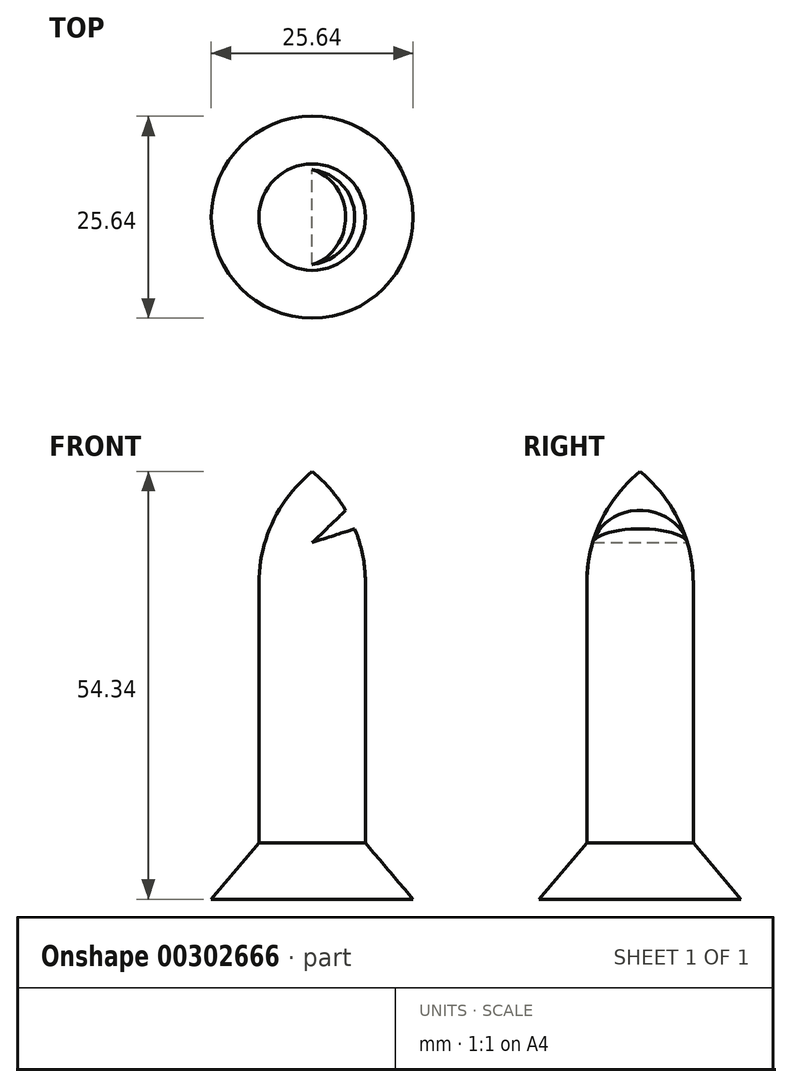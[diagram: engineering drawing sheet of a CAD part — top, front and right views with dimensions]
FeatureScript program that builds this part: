
annotation { "Feature Type Name" : "Feature", "Feature Type Description" : "" }
export const myFeature = defineFeature(function(context is Context, id is Id, definition is map)
    precondition{}
    {
        {
            var Q0;
            Q0=qCreatedBy(makeId("Front.planeOp"),FACE);
            var sketch = newSketch(context, id + "F0", { "sketchPlane" : qUnion([Q0])});
            skLineSegment(sketch, "E0", {"start": v(0, 0) * mm, "end": v(0, 0) * mm});
            skLineSegment(sketch, "E1", {"start": v(0, 54.34) * mm, "end": v(0, 0) * mm});
            skLineSegment(sketch, "E2", {"start": v(0, 40.14) * mm, "end": v(6.76, 40.14) * mm});
            skLineSegment(sketch, "E3", {"start": v(6.76, 40.14) * mm, "end": v(6.76, 7.16) * mm});
            skLineSegment(sketch, "E4", {"start": v(6.76, 7.16) * mm, "end": v(12.82, 0) * mm});
            skLineSegment(sketch, "E5", {"start": v(12.82, 0) * mm, "end": v(0, 0) * mm});
            skArc(sketch, "E6", {"start": v(6.76, 40.14) * mm, "mid": v(4.98, 48) * mm, "end": v(0, 54.34) * mm});
            skSolve(sketch);
        }
        {
            var Q0;
            Q0 = qSketchRegion(id + "F0", true);
            var Q1;
            Q1=sQuery(id+"F0.wireOp",EDGE,"E1");
            revolve(context, id + "F1", {"entities" : qUnion([Q0]), "axis" : qUnion([Q1]), "revolveType" : RevolveType.FULL});
        }
        {
            var Q0;
            Q0=qCreatedBy(makeId("Front.planeOp"),FACE);
            var sketch = newSketch(context, id + "F2", { "sketchPlane" : qUnion([Q0])});
            skLineSegment(sketch, "E7", {"start": v(0, 45.33) * mm, "end": v(5.38, 50.49) * mm});
            skLineSegment(sketch, "E8", {"start": v(5.38, 50.49) * mm, "end": v(7.02, 47.58) * mm});
            skLineSegment(sketch, "E9", {"start": v(7.02, 47.58) * mm, "end": v(0, 45.33) * mm});
            skSolve(sketch);
        }
        {
            var Q0;
            Q0 = qSketchRegion(id + "F2", true);
            extrude(context, id + "F3", {"entities" : qUnion([Q0]), "operationType" : NewBodyOperationType.REMOVE, "depth" : 19.05 * mm, "hasSecondDirection" : true, "secondDirectionOppositeDirection" : true, "secondDirectionDepth" : 25.4 * mm});
        }
    });
